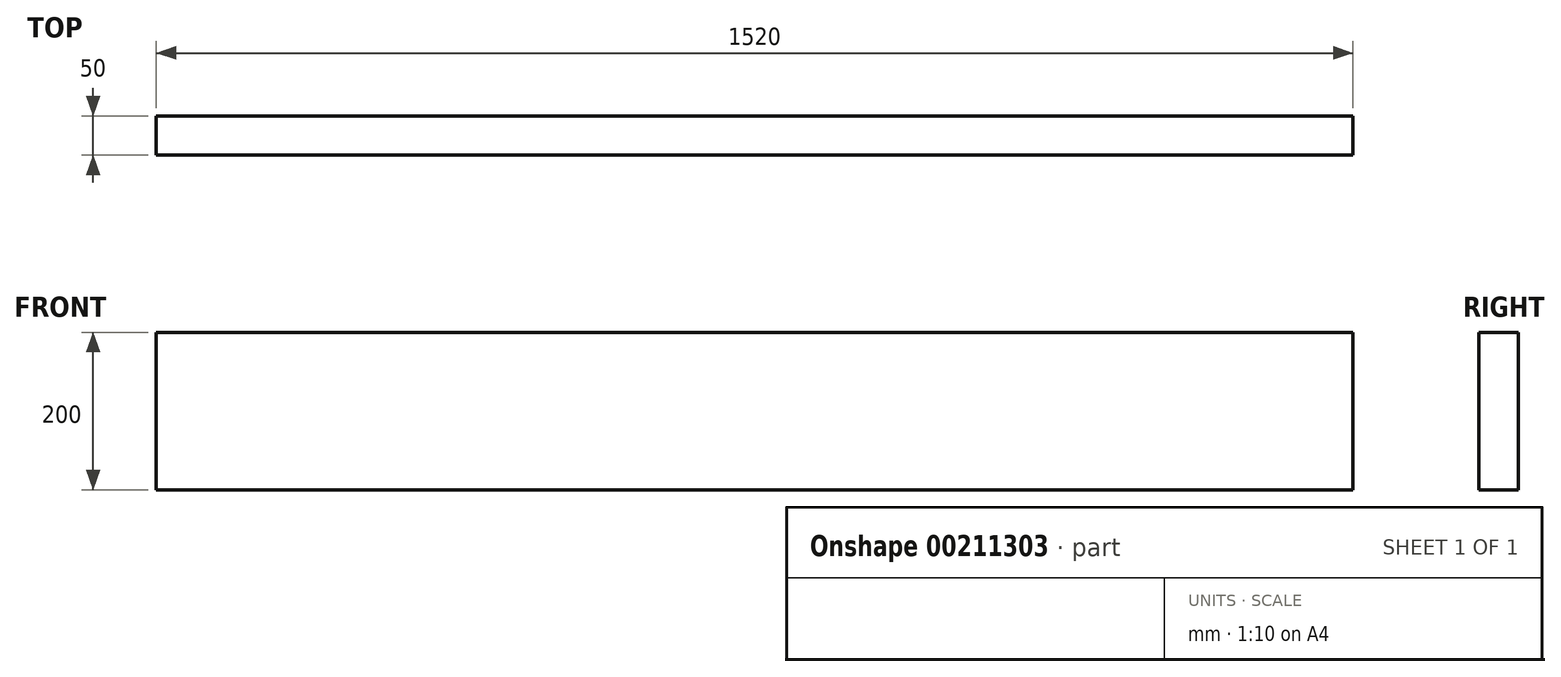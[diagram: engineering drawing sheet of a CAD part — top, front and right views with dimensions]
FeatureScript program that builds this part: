
annotation { "Feature Type Name" : "Feature", "Feature Type Description" : "" }
export const myFeature = defineFeature(function(context is Context, id is Id, definition is map)
    precondition{}
    {
        {
            var Q0;
            Q0=qCreatedBy(makeId("Top.planeOp"),FACE);
            var sketch = newSketch(context, id + "F0", { "sketchPlane" : qUnion([Q0])});
            skLineSegment(sketch, "E0.bottom", {"start": v(-759.54, -136.1) * mm, "end": v(760.46, -136.1) * mm});
            skLineSegment(sketch, "E0.top", {"start": v(-759.54, -186.1) * mm, "end": v(760.46, -186.1) * mm});
            skLineSegment(sketch, "E0.left", {"start": v(-759.54, -136.1) * mm, "end": v(-759.54, -186.1) * mm});
            skLineSegment(sketch, "E0.right", {"start": v(760.46, -136.1) * mm, "end": v(760.46, -186.1) * mm});
            skSolve(sketch);
        }
        {
            var Q0;
            Q0=makeQuery(id+"F0.imprint","IMPRINT",FACE,{"disambiguationData":[TD([[makeQuery(id+"F0.imprint","IMPRINT",EDGE,{"derivedFrom":sQuery(id+"F0.wireOp",EDGE,"E0.bottom")}),-1.0]])]});
            extrude(context, id + "F1", {"entities" : qUnion([Q0]), "depth" : 200 * mm});
        }
    });
